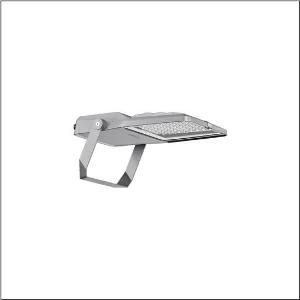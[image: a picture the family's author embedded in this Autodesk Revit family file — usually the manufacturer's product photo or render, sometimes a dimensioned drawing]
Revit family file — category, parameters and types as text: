
# Revit family: floodlight_fl_21_iq_mini___rs12_5xa7771c4b1a_004d
name_source: partatom
category: Lighting Fixtures
units: mm (PartAtom-declared; Revit-internal decimal feet)

## family parameters
Cut with Voids When Loaded = No
Host = Face
Light Source = No
Part Type = Normal
Room Calculation Point = No
Round Connector Dimension = Use Diameter
Shared = No

## types (1)
- --- (1 x LED, 12860 lm, 87.2 W, 4000K)
    Apparent Load = 87 VA
    CIE Flux Codes = 79 92 99 100 100
    Color Rendering = 70
    Color Temperature = 4000K
    Default Elevation = 1800 mm
    Description = Floodlight FL 21 iQ mini, floodlight, primary light control with lens, of PMMA, primary optical cover: protective disc, of toughened safety glass, transparent, light distribution: RS12, light emission: direct distribution, installation type: surface-mounted, LED, High Power LED, rated luminous flux: 12.860lm, luminous efficacy: 148lm/W, light colour: 740, colour temperature: 4000K, control: Auto-Match, Temp-Guard, Lumen-Switch, Night-Set, Smart-Wire, Light-Fading, Desk-Remote (wireless, voltage-free reading and setting of iQ features in the workshop via application-optimized NFC function/RFID function), optimised constant luminous flux control (CLO 2.0), with terminal, 6-pole, mains connection: 220..240V, AC, 50/60Hz, start of lifetime: 87W, end of service life: 92W, reduction: 40W, luminaire housing, of diecast aluminium, powder-coated, Siteco® metallic grey (DB 702S), corrosivity category C5 mid according to DIN EN ISO 12944, sealing non-destructively replaceable, mounting bracket, of steel, galvanised, powder-coated, Siteco® metallic grey (DB 702S), protection rating (complete): IP66, insulation class (complete): insulation class II (safety insulation), certification: CE, ENEC, VDE, protection symbol: D, impact resistance: IK08, permissible operating ambient temperature: -40..+40°C, permissible operating ambient temperature for outdoor applications: -40..+50°C, standard: DIN EN 12944, LABS conformity tested according to VDMA 24364:2018-05, packaging unit: 1 piece

Light Distribution: RS12
    Height = 70 mm
    Lamp = 1 x LED
    Lamp Light Flux = 12860 lm
    Lamp Power = 87.2 W
    Lamp count = 1
    Length = 485 mm
    Luminous efficacy = 147 lm/W
    Manufacturer = Siteco
    ModVariant = No
    Model = 5XA7771C4B1A
    Number of Poles = 1
    OnlyDefault = Yes
    Power Factor = 1
    Product Name = Floodlight FL 21 iQ mini | RS12
    Product group = floodlight | pylon annexe
    ProductGroupID = 6200
    Protection Class = Protection class II
    Protection Degree = IP 66
    RLX_Detail_Level = 1
    RLX_Emergency_Light_Flux = 0 lm
    RLX_Emergency_Type = 0
    RLX_Emergency_Type_DB = No
    RlxData = <blob elided: 91065 chars, md5=e8fcc845>
    Socket = socket
    Standby Power = 0 W
    System Light Flux = 12860 lm
    System Power = 87 W
    Type Comments = factory setting: luminous flux: 100 % | dim-lin: 254 | 456 mA
    Type Image = l_1006845.jpg
    URL = http://relux.com
    VarID = @adj_117875
    Voltage = 0 V
    Weight = 0.00 kg
    Width = 337 mm

## geometry (parser evidence)
native form markers: Blend x4, Sweep x12
no freeform markers — native parametric forms only
